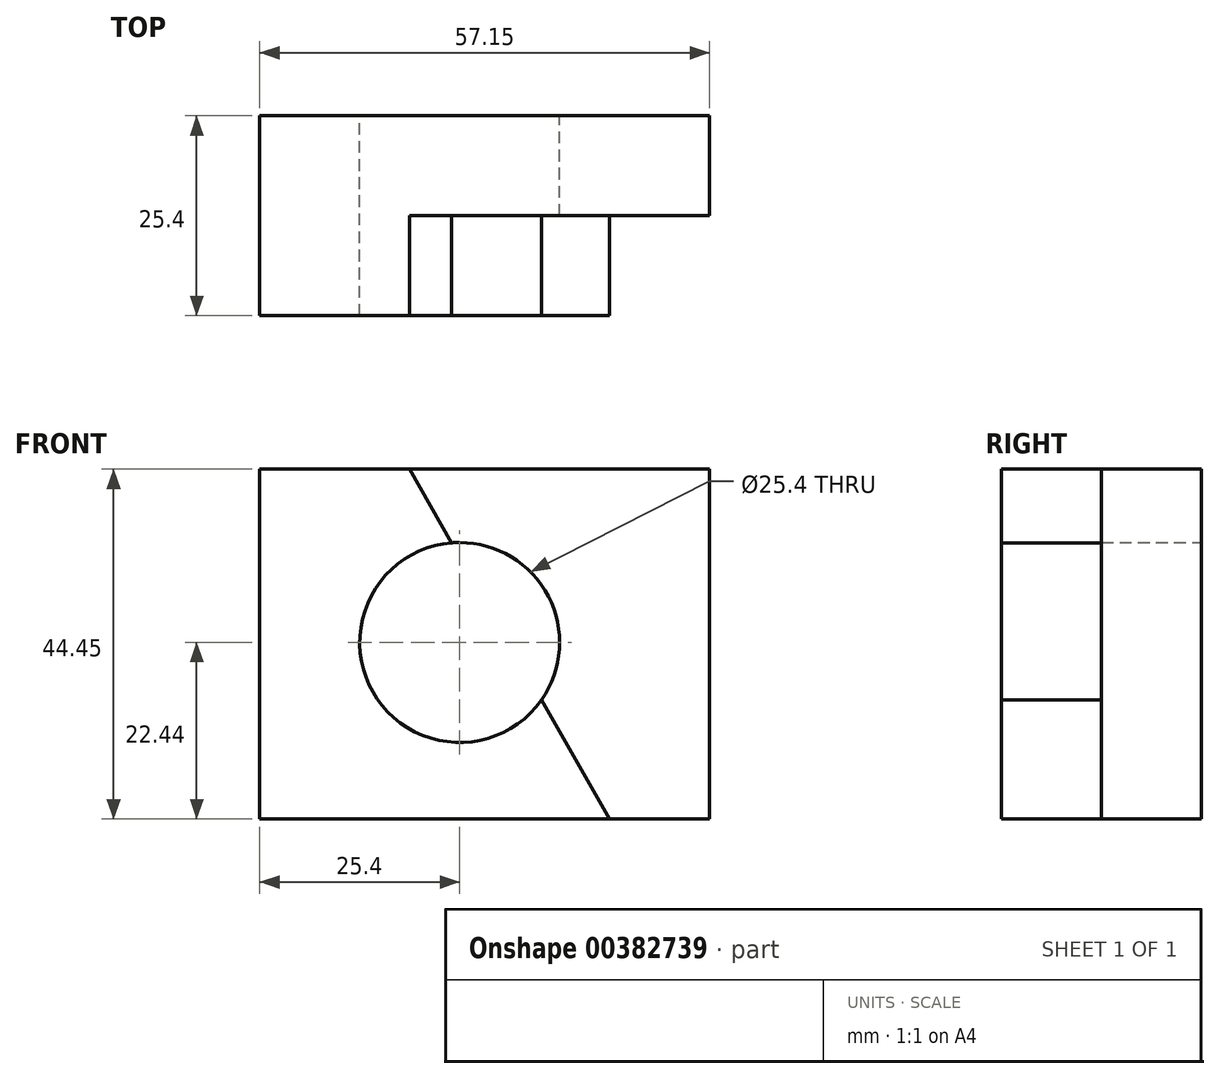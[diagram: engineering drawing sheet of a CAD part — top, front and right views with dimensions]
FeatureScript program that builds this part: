
annotation { "Feature Type Name" : "Feature", "Feature Type Description" : "" }
export const myFeature = defineFeature(function(context is Context, id is Id, definition is map)
    precondition{}
    {
        {
            var Q0;
            Q0=qCreatedBy(makeId("Top.planeOp"),FACE);
            var sketch = newSketch(context, id + "F0", { "sketchPlane" : qUnion([Q0])});
            skLineSegment(sketch, "E0.bottom", {"start": v(0, 0) * mm, "end": v(57.15, 0) * mm});
            skLineSegment(sketch, "E0.top", {"start": v(0, 25.4) * mm, "end": v(57.15, 25.4) * mm});
            skLineSegment(sketch, "E0.left", {"start": v(0, 0) * mm, "end": v(0, 25.4) * mm});
            skLineSegment(sketch, "E0.right", {"start": v(57.15, 0) * mm, "end": v(57.15, 25.4) * mm});
            skSolve(sketch);
        }
        {
            var Q0;
            Q0=makeQuery(id+"F0.imprint","IMPRINT",FACE,{"disambiguationData":[TD([[makeQuery(id+"F0.imprint","IMPRINT",EDGE,{"derivedFrom":sQuery(id+"F0.wireOp",EDGE,"E0.bottom")}),1.0]])]});
            extrude(context, id + "F1", {"entities" : qUnion([Q0]), "depth" : 44.45 * mm});
        }
        {
            var Q0;
            Q0=makeQuery(id+"F1.opExtrude","SWEPT_FACE",FACE,{"disambiguationData":[OSD([sQuery(id+"F0.wireOp",EDGE,"E0.bottom")])]});
            var sketch = newSketch(context, id + "F2", { "sketchPlane" : qUnion([Q0])});
            skLineSegment(sketch, "E1", {"start": v(19.05, 44.45) * mm, "end": v(44.45, 0) * mm});
            skSolve(sketch);
        }
        {
            var Q0;
            {var subQ0=sQuery(id+"F2.wireOp",EDGE,"E1");Q0=makeQuery(id+"F2.imprint","IMPRINT",FACE,{"disambiguationData":[TD([[makeQuery(id+"F2.imprint","IMPRINT",EDGE,{"derivedFrom":subQ0}),1.0]])]});}
            extrude(context, id + "F3", {"entities" : qUnion([Q0]), "operationType" : NewBodyOperationType.REMOVE, "oppositeDirection" : true, "depth" : 12.7 * mm});
        }
        {
            var Q0;
            Q0=makeQuery(id+"F1.opExtrude","SWEPT_FACE",FACE,{"disambiguationData":[OSD([sQuery(id+"F0.wireOp",EDGE,"E0.top")])]});
            var sketch = newSketch(context, id + "F4", { "sketchPlane" : qUnion([Q0])});
            skCircle(sketch, "E2", {"center": v(-25.4, 22.44) * mm, "radius": 12.7 * mm});
            skSolve(sketch);
        }
        {
            var Q0;
            Q0=makeQuery(id+"F4.imprint","IMPRINT",FACE,{"disambiguationData":[TD([[makeQuery(id+"F4.imprint","IMPRINT",EDGE,{"derivedFrom":sQuery(id+"F4.wireOp",EDGE,"E2")}),1.0]])]});
            extrude(context, id + "F5", {"entities" : qUnion([Q0]), "operationType" : NewBodyOperationType.REMOVE, "oppositeDirection" : true, "depth" : 25.4 * mm});
        }
    });
